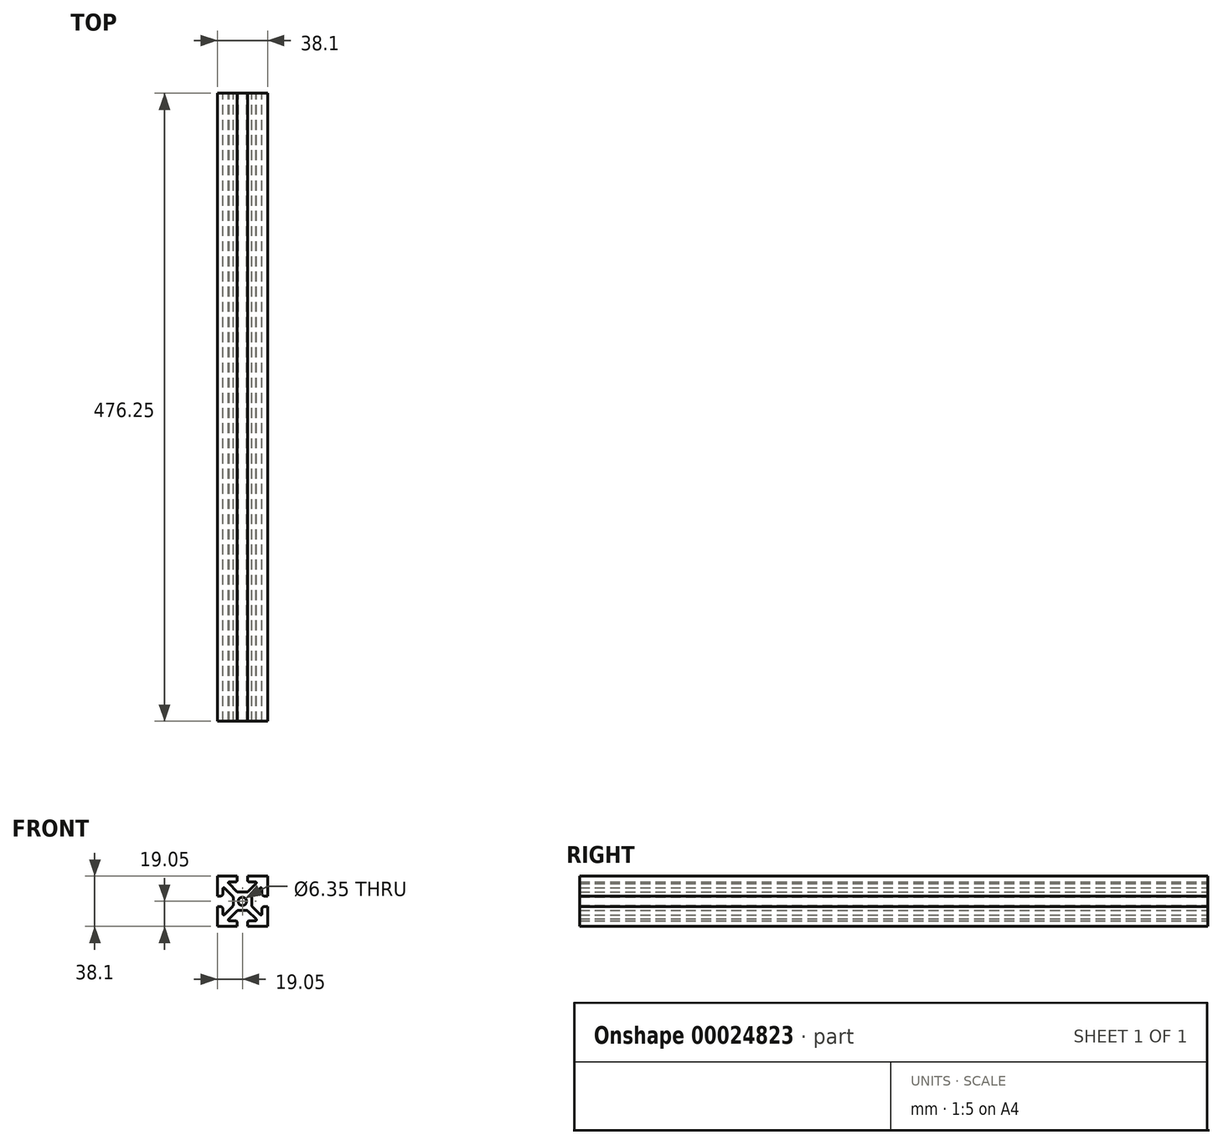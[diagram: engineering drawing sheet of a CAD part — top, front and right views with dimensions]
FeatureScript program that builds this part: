
annotation { "Feature Type Name" : "Feature", "Feature Type Description" : "" }
export const myFeature = defineFeature(function(context is Context, id is Id, definition is map)
    precondition{}
    {
        {
            var Q0;
            Q0=qCreatedBy(makeId("Front.planeOp"),FACE);
            var sketch = newSketch(context, id + "F0", { "sketchPlane" : qUnion([Q0])});
            skLineSegment(sketch, "E0", {"start": v(19.05, 19.05) * mm, "end": v(-19.05, 19.05) * mm});
            skLineSegment(sketch, "E1", {"start": v(-19.05, 19.05) * mm, "end": v(-19.05, -19.05) * mm});
            skLineSegment(sketch, "E2", {"start": v(-19.05, -19.05) * mm, "end": v(19.05, -19.05) * mm});
            skLineSegment(sketch, "E3", {"start": v(19.05, -19.05) * mm, "end": v(19.05, 19.05) * mm});
            skSolve(sketch);
        }
        {
            var Q0;
            Q0=makeQuery(id+"F0.imprint","IMPRINT",FACE,{"disambiguationData":[TD([[makeQuery(id+"F0.imprint","IMPRINT",EDGE,{"derivedFrom":sQuery(id+"F0.wireOp",EDGE,"E0")}),1.0]])]});
            extrude(context, id + "F1", {"entities" : qUnion([Q0]), "depth" : 476.25 * mm});
        }
        {
            var Q0;
            Q0=qCreatedBy(makeId("Front.planeOp"),FACE);
            var sketch = newSketch(context, id + "F2", { "sketchPlane" : qUnion([Q0])});
            skLineSegment(sketch, "E4", {"start": v(-4.06, 19.05) * mm, "end": v(-4.06, 15.65) * mm});
            skLineSegment(sketch, "E5", {"start": v(-4.86, 14.86) * mm, "end": v(-9.78, 14.86) * mm});
            skLineSegment(sketch, "E6", {"start": v(0, 6.99) * mm, "end": v(0, 19.05) * mm});
            skLineSegment(sketch, "E7", {"start": v(0, 19.05) * mm, "end": v(-4.06, 19.05) * mm});
            skPoint(sketch, "E8.visualSharp", {"position": v(-10.29, 14.86) * mm});
            skArc(sketch, "E8.filletArc", {"start": v(-9.78, 14.86) * mm, "mid": v(-10.56, 14.25) * mm, "end": v(-10.14, 13.36) * mm});
            skPoint(sketch, "E9.visualSharp", {"position": v(-4.06, 14.86) * mm});
            skArc(sketch, "E9.filletArc", {"start": v(-4.86, 14.86) * mm, "mid": v(-4.3, 15.1) * mm, "end": v(-4.06, 15.65) * mm});
            skLineSegment(sketch, "E10", {"start": v(-10.14, 13.36) * mm, "end": v(-4.23, 7.45) * mm});
            skLineSegment(sketch, "E11", {"start": v(-3.11, 6.99) * mm, "end": v(0, 6.99) * mm});
            skPoint(sketch, "E12.visualSharp", {"position": v(-3.77, 6.99) * mm});
            skArc(sketch, "E12.filletArc", {"start": v(-4.23, 7.45) * mm, "mid": v(-3.72, 7.1) * mm, "end": v(-3.11, 6.99) * mm});
            skSolve(sketch);
        }
        {
            var Q0;
            Q0=makeQuery(id+"F2.imprint","IMPRINT",FACE,{"disambiguationData":[TD([[makeQuery(id+"F2.imprint","IMPRINT",EDGE,{"derivedFrom":sQuery(id+"F2.wireOp",EDGE,"E4")}),1.0]])]});
            extrude(context, id + "F3", {"entities" : qUnion([Q0]), "operationType" : NewBodyOperationType.REMOVE, "endBound" : BoundingType.UP_TO_NEXT, "depth" : 25.4 * mm});
        }
        {
            var Q0;
            Q0=makeQuery(id+"F1.opExtrude","SWEPT_BODY",BODY,{"disambiguationData":[OSD([sQuery(id+"F0.wireOp",EDGE,"E0"),sQuery(id+"F0.wireOp",EDGE,"E1"),sQuery(id+"F0.wireOp",EDGE,"E2"),sQuery(id+"F0.wireOp",EDGE,"E3")])]});
            var Q1;
            Q1=qCreatedBy(makeId("Right.planeOp"),FACE);
            mirror(context, id + "F4", {"operationType" : NewBodyOperationType.INTERSECT, "entities" : qUnion([Q0]), "mirrorPlane" : qUnion([Q1])});
        }
        {
            var Q0;
            Q0=qCreatedBy(makeId("Top.planeOp"),FACE);
            var sketch = newSketch(context, id + "F5", { "sketchPlane" : qUnion([Q0])});
            skLineSegment(sketch, "E13", {"start": v(0, 140.49) * mm, "end": v(0, 18.47) * mm});
            skSolve(sketch);
        }
        {
            var Q0;
            Q0=makeQuery(id+"F1.opExtrude","SWEPT_BODY",BODY,{"disambiguationData":[OSD([sQuery(id+"F0.wireOp",EDGE,"E0"),sQuery(id+"F0.wireOp",EDGE,"E1"),sQuery(id+"F0.wireOp",EDGE,"E2"),sQuery(id+"F0.wireOp",EDGE,"E3")])]});
            var Q1;
            Q1=qCreatedBy(makeId("Top.planeOp"),FACE);
            mirror(context, id + "F6", {"operationType" : NewBodyOperationType.INTERSECT, "entities" : qUnion([Q0]), "mirrorPlane" : qUnion([Q1])});
        }
        {
            var Q0;
            Q0=qCreatedBy(makeId("Front.planeOp"),FACE);
            var sketch = newSketch(context, id + "F7", { "sketchPlane" : qUnion([Q0])});
            skLineSegment(sketch, "E14", {"start": v(-19.05, 4.06) * mm, "end": v(-16.45, 4.06) * mm});
            skLineSegment(sketch, "E15", {"start": v(-14.86, 5.65) * mm, "end": v(-14.86, 9.5) * mm});
            skLineSegment(sketch, "E16", {"start": v(-13.5, 10.05) * mm, "end": v(-7.45, 4) * mm});
            skLineSegment(sketch, "E17", {"start": v(-6.99, 2.88) * mm, "end": v(-6.99, 0) * mm});
            skLineSegment(sketch, "E18", {"start": v(-6.99, 0) * mm, "end": v(-19.05, 0) * mm});
            skLineSegment(sketch, "E19", {"start": v(-19.05, 0) * mm, "end": v(-19.05, 4.06) * mm});
            skPoint(sketch, "E20.visualSharp", {"position": v(-14.86, 4.06) * mm});
            skArc(sketch, "E20.filletArc", {"start": v(-16.45, 4.06) * mm, "mid": v(-15.32, 4.53) * mm, "end": v(-14.86, 5.65) * mm});
            skArc(sketch, "E21.filletArc", {"start": v(-13.5, 10.05) * mm, "mid": v(-14.37, 10.23) * mm, "end": v(-14.86, 9.5) * mm});
            skArc(sketch, "E22.filletArc", {"start": v(-6.99, 2.88) * mm, "mid": v(-7.1, 3.49) * mm, "end": v(-7.45, 4) * mm});
            skSolve(sketch);
        }
        {
            var Q0;
            Q0=makeQuery(id+"F7.imprint","IMPRINT",FACE,{"disambiguationData":[TD([[makeQuery(id+"F7.imprint","IMPRINT",EDGE,{"derivedFrom":sQuery(id+"F7.wireOp",EDGE,"E14")}),-1.0]])]});
            extrude(context, id + "F8", {"entities" : qUnion([Q0]), "operationType" : NewBodyOperationType.REMOVE, "endBound" : BoundingType.UP_TO_NEXT, "depth" : 25.4 * mm});
        }
        {
            var Q0;
            Q0=makeQuery(id+"F1.opExtrude","SWEPT_BODY",BODY,{"disambiguationData":[OSD([sQuery(id+"F0.wireOp",EDGE,"E0"),sQuery(id+"F0.wireOp",EDGE,"E1"),sQuery(id+"F0.wireOp",EDGE,"E2"),sQuery(id+"F0.wireOp",EDGE,"E3")])]});
            var Q1;
            Q1=qCreatedBy(makeId("Top.planeOp"),FACE);
            mirror(context, id + "F9", {"operationType" : NewBodyOperationType.INTERSECT, "entities" : qUnion([Q0]), "mirrorPlane" : qUnion([Q1])});
        }
        {
            var Q0;
            Q0=makeQuery(id+"F1.opExtrude","SWEPT_BODY",BODY,{"disambiguationData":[OSD([sQuery(id+"F0.wireOp",EDGE,"E0"),sQuery(id+"F0.wireOp",EDGE,"E1"),sQuery(id+"F0.wireOp",EDGE,"E2"),sQuery(id+"F0.wireOp",EDGE,"E3")])]});
            var Q1;
            Q1=qCreatedBy(makeId("Right.planeOp"),FACE);
            mirror(context, id + "F10", {"operationType" : NewBodyOperationType.INTERSECT, "entities" : qUnion([Q0]), "mirrorPlane" : qUnion([Q1])});
        }
        {
            var Q0;
            Q0=qCreatedBy(makeId("Front.planeOp"),FACE);
            var sketch = newSketch(context, id + "F11", { "sketchPlane" : qUnion([Q0])});
            skCircle(sketch, "E23", {"center": v(0, 0) * mm, "radius": 3.17 * mm});
            skSolve(sketch);
        }
        {
            var Q0;
            Q0=makeQuery(id+"F11.imprint","IMPRINT",FACE,{"disambiguationData":[TD([[makeQuery(id+"F11.imprint","IMPRINT",EDGE,{"derivedFrom":sQuery(id+"F11.wireOp",EDGE,"E23")}),1.0]])]});
            extrude(context, id + "F12", {"entities" : qUnion([Q0]), "operationType" : NewBodyOperationType.REMOVE, "endBound" : BoundingType.UP_TO_NEXT, "depth" : 25.4 * mm});
        }
    });
